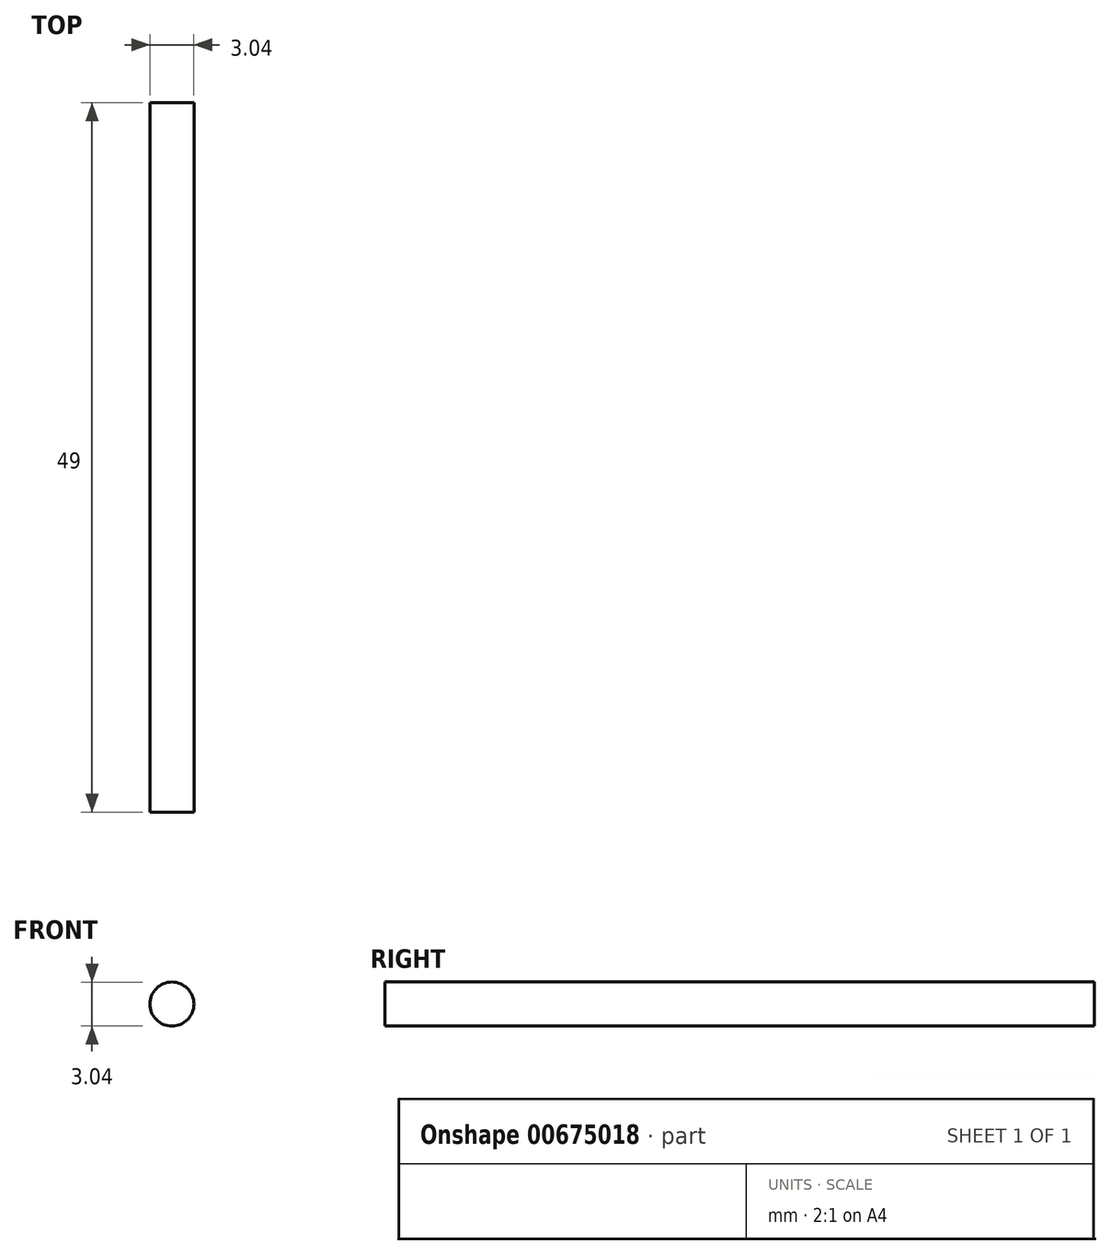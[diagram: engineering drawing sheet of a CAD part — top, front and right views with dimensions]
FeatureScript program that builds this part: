
annotation { "Feature Type Name" : "Feature", "Feature Type Description" : "" }
export const myFeature = defineFeature(function(context is Context, id is Id, definition is map)
    precondition{}
    {
        {
            var Q0;
            Q0=qCreatedBy(makeId("Front.planeOp"),FACE);
            var sketch = newSketch(context, id + "F0", { "sketchPlane" : qUnion([Q0])});
            skCircle(sketch, "E0", {"center": v(0, 0) * mm, "radius": 1.52 * mm});
            skSolve(sketch);
        }
        {
            var Q0;
            Q0=makeQuery(id+"F0.imprint","IMPRINT",FACE,{"disambiguationData":[TD([[makeQuery(id+"F0.imprint","IMPRINT",EDGE,{"derivedFrom":sQuery(id+"F0.wireOp",EDGE,"E0")}),1.0]])]});
            extrude(context, id + "F1", {"entities" : qUnion([Q0]), "oppositeDirection" : true, "depth" : 49 * mm, "offsetDistance" : 25 * mm});
        }
    });
